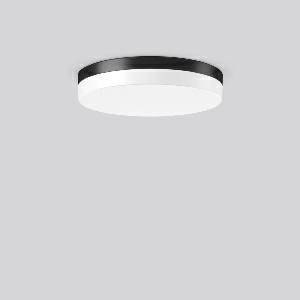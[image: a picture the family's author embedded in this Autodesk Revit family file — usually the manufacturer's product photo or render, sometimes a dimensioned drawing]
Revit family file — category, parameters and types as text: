
# Revit family: flat_slim_round_312632_0031_76_b1a7
name_source: partatom
category: Lighting Fixtures
units: mm (PartAtom-declared; Revit-internal decimal feet)

## family parameters
Cut with Voids When Loaded = No
Host = Face
Light Source = No
Part Type = Normal
Room Calculation Point = No
Round Connector Dimension = Use Diameter
Shared = No

## types (1)
- MultiLumen 1 830 (1 x LED Modul 830, 2400 lm, 3000)
    Apparent Load = 20 VA
    CIE Flux Codes = 39 70 90 83 100
    Color Rendering = 80
    Color Temperature = 3000
    Default Elevation = 1800 mm
    Height = 70 mm
    Lamp = 1 x LED Modul 830
    Lamp Light Flux = 2400 lm
    Lamp count = 1
    Length = 400 mm
    Lifetime = 50000 h
    Luminous efficacy = 120 lm/W
    Manufacturer = RZB
    ModVariant = No
    Model = 312632.0031.76
    Mounting Place = Ceiling
    Mounting Type = Surface mounted
    Number of Poles = 1
    OnlyDefault = Yes
    Power Factor = 1
    Product Name = FLAT SLIM round
    Product group = Surface mounted ceiling and wall luminaires
    ProductGroupID = 305
    Protection Class = Protection class I
    Protection Degree = Degree of protection
    RLX_Detail_Level = 1
    RLX_Emergency_Light_Flux = 0 lm
    RLX_Emergency_Type = 0
    RLX_Emergency_Type_DB = No
    RlxData = <blob elided: 21237 chars, md5=2b897f16>
    Socket = socket
    Standby Power = 0 W
    System Light Flux = 2400 lm
    System Power = 20 W
    Type Comments = MultiLumen 1 830
    Type Image = 312631.0031.jpg
    URL = http://relux.com
    VarID = multilumen_1_830
    Voltage = 0 V
    Weight = 0.00 kg
    Width = 0 mm  [stored 0 ft]

note: [stored X ft] marks values corroborated as IEEE doubles in the binary element streams (Revit-internal decimal feet)

## geometry (parser evidence)
native form markers: Blend x4, Sweep x12
no freeform markers — native parametric forms only
